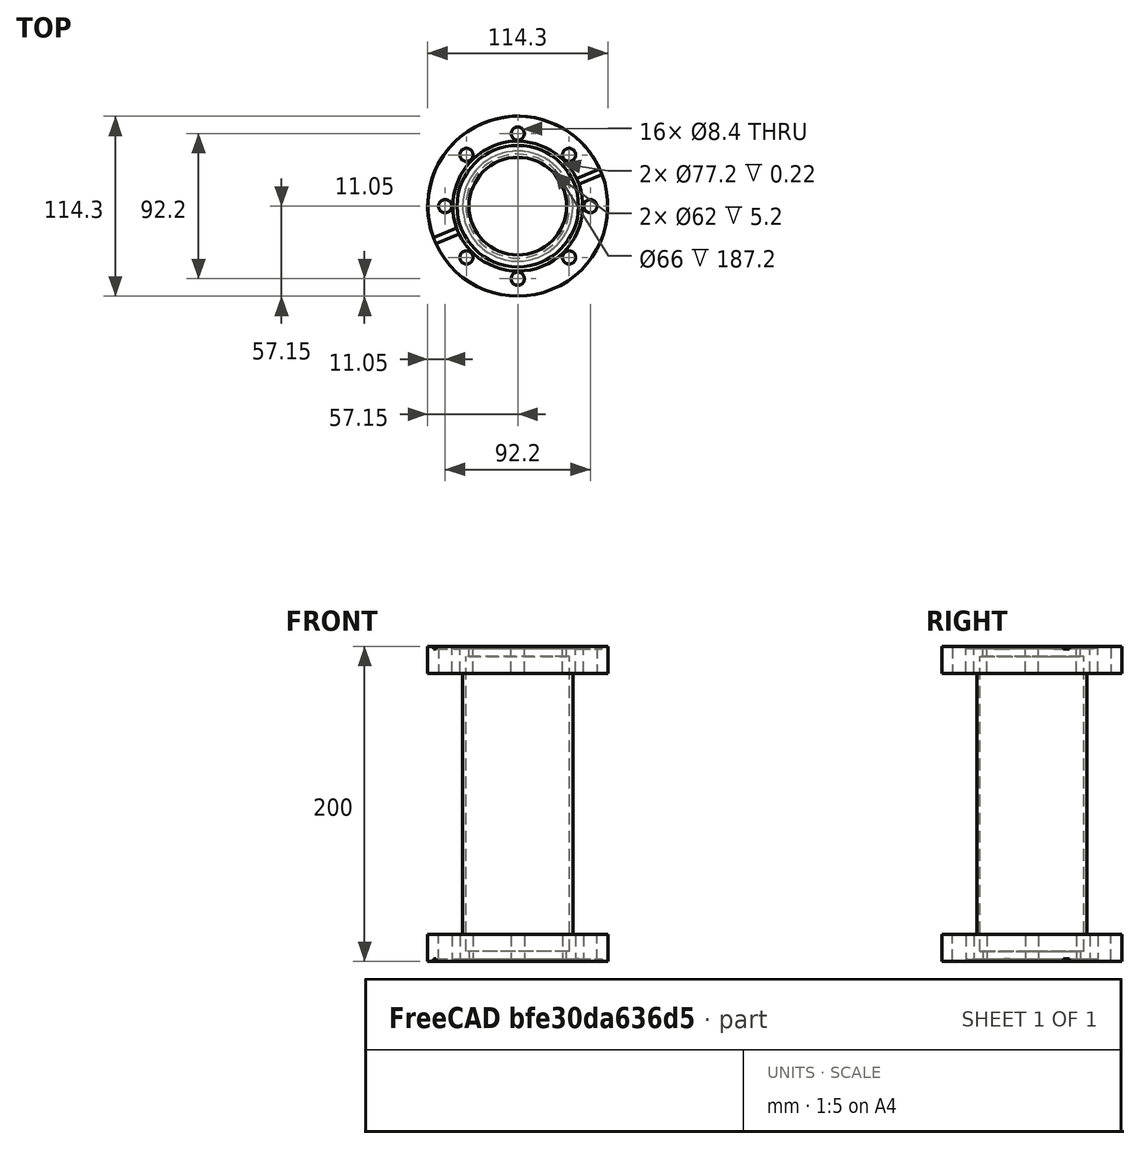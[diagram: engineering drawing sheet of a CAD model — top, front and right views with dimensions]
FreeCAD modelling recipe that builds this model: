
FCSTD DOCUMENT  (FreeCAD 0.21R0.21.2)
Label: CFPipeStraight_NonRotatable
License: All rights reserved
LicenseURL: http://en.wikipedia.org/wiki/All_rights_reserved
objects: Part::Cylinder×14, Part::Cut×12, Part::MultiFuse×7, Part::Box×4, Part::FeaturePython×3, Part::Cone×2, Spreadsheet::Sheet×1, Part::Compound×1
note: 41 computed .brp shape members not serialized (recipe doc carries the construction recipe); baked Part::Feature solids carry a one-line shape summary decoded from their .brp

FEATURE [Part::Box] Box002  label="Cube002"
  AttacherType = Attacher::AttachEngine3D
  Height = 1.5
  Length = 16.9
  Placement = pos=(40.75,-2,0) rot=(0,0,1;0rad)
  Width = 4
  expr: .Placement.Base.x = <<ConflatFlange>>.cf_sealrecess / 2 - 0.5
  expr: .Placement.Base.y = -2
  expr: Length = (<<ConflatFlange>>.cf_od - <<ConflatFlange>>.cf_sealrecess) / 2 + 1
FEATURE [Part::Box] Box003  label="Cube003"
  AttacherType = Attacher::AttachEngine3D
  Height = 1.5
  Length = 16.9
  Placement = pos=(-57.65,-2,0) rot=(0,0,1;0rad)
  Width = 4
  expr: .Placement.Base.x = -<<ConflatFlange>>.cf_sealrecess / 2 + 0.5 - ((<<ConflatFlange>>.cf_od - <<ConflatFlange>>.cf_sealrecess) / 2 + 1)
  expr: .Placement.Base.y = -2
  expr: Length = (<<ConflatFlange>>.cf_od - <<ConflatFlange>>.cf_sealrecess) / 2 + 1
FEATURE [Part::Cone] Cone004
  Angle = 360
  AttacherType = Attacher::AttachEngine3D
  Height = 0.22
  Radius1 = 38.6
  Radius2 = 41.25
  expr: Height = 1.2 - 0.98
  expr: Radius1 = <<ConflatFlange>>.cf_knife / 2
  expr: Radius2 = <<ConflatFlange>>.cf_sealrecess / 2
FEATURE [Part::Cylinder] Cylinder018
  Angle = 360
  AttacherType = Attacher::AttachEngine3D
  FirstAngle = 0
  Height = 10.6
  Placement = pos=(0,0,6.4) rot=(0,0,1;0rad)
  Radius = 35
  SecondAngle = 0
  expr: .Placement.Base.z = <<ConflatFlange>>.cf_pipedepth
  expr: Height = <<ConflatFlange>>.cf_thickness - <<ConflatFlange>>.cf_pipedepth
  expr: Radius = <<ConflatFlange>>.cf_maxtubedia / 2
FEATURE [Part::Cylinder] Cylinder019
  Angle = 360
  AttacherType = Attacher::AttachEngine3D
  FirstAngle = 0
  Height = 17
  Radius = 31
  SecondAngle = 0
  expr: Height = <<ConflatFlange>>.cf_thickness
  expr: Radius = <<ConflatFlange>>.cf_maxtubedia / 2 - 2 * <<ConflatFlange>>.cf_pipe_wallwidth
FEATURE [Part::Cylinder] Cylinder020  label="Blank004"
  Angle = 360
  AttacherType = Attacher::AttachEngine3D
  FirstAngle = 0
  Height = 17
  Radius = 57.15
  SecondAngle = 0
  expr: Height = <<ConflatFlange>>.cf_thickness
  expr: Radius = <<ConflatFlange>>.cf_od / 2
FEATURE [Part::Cylinder] Cylinder021  label="SealRecess004"
  Angle = 360
  AttacherType = Attacher::AttachEngine3D
  FirstAngle = 0
  Height = 1.2
  Radius = 41.25
  SecondAngle = 0
  expr: Radius = <<ConflatFlange>>.cf_sealrecess / 2
FEATURE [Part::Cut] Cut015
  Base = -> Cylinder020
  Tool = -> Cylinder021
FEATURE [Part::Cylinder] Cylinder022
  Angle = 360
  AttacherType = Attacher::AttachEngine3D
  FirstAngle = 0
  Height = 0.22
  Radius = 38.6
  SecondAngle = 0
  expr: Height = 1.2 - 0.98
  expr: Radius = <<ConflatFlange>>.cf_knife / 2
FEATURE [Part::Cut] Cut016  label="KnifeEdge004"
  Base = -> Cone004
  Placement = pos=(0,0,0.98) rot=(0,0,1;0rad)
  Tool = -> Cylinder022
FEATURE [Part::Cylinder] Cylinder023
  Angle = 360
  AttacherType = Attacher::AttachEngine3D
  FirstAngle = 0
  Height = 17
  Placement = pos=(46.1,0,0) rot=(0,0,1;0rad)
  Radius = 4.2
  SecondAngle = 0
  expr: .Placement.Base.x = <<ConflatFlange>>.cf_boltcircle / 2
  expr: Height = <<ConflatFlange>>.cf_thickness
  expr: Radius = <<ConflatFlange>>.cf_boltdia / 2
FEATURE [Part::FeaturePython] Array004  label="BoltHoleArray004"  # Draft array (typed FeaturePython)
  AlwaysSyncPlacement = false
  Angle = 360
  ArrayType = 1
  Axis = (0,0,1)
  Base = -> Cylinder023
  Center = (0,0,0)
  Count = 8
  ExpandArray = false
  Fuse = false
  IntervalAxis = (0,0,0)
  IntervalX = (50,0,0)
  IntervalY = (0,50,0)
  IntervalZ = (0,0,50)
  NumberCircles = 3
  NumberPolar = 8
  NumberX = 2
  NumberY = 2
  NumberZ = 1
  PlacementList = 8 placements: [(46.1,0,0),(32.5976,32.5976,0),(1.02363e-14,46.1,0),(-32.5976,32.5976,0),(-46.1,5.64562e-15,0),(-32.5976,-32.5976,0),(-1.02363e-14,-46.1,0),(32.5976,-32.5976,0)]
  RadialDistance = 50
  ScaleList = (8) [(1,1,1),(1,1,1),(1,1,1),(1,1,1),(1,1,1),(1,1,1),(1,1,1),(1,1,1)]
  Symmetry = 1
  TangentialDistance = 25
  expr: NumberPolar = <<ConflatFlange>>.cf_nbolts
FEATURE [Part::Cylinder] Cylinder025
  Angle = 360
  AttacherType = Attacher::AttachEngine3D
  FirstAngle = 0
  Height = 1.5
  Radius = 41.25
  SecondAngle = 0
  expr: Radius = <<ConflatFlange>>.cf_sealrecess / 2
FEATURE [Part::MultiFuse] Fusion005  label="UndrilledBlank004"
  Shapes = -> [Cut015,Cut016]
FEATURE [Part::Cut] Cut017  label="BlankFlange_NonRotatable002"
  Base = -> Fusion005
  Tool = -> Array004
FEATURE [Part::MultiFuse] Fusion006
  Shapes = -> [Cylinder019,Cylinder018]
FEATURE [Part::Cut] Cut018  label="WeldFlange_NonRotatable_NoGrooves"
  Base = -> Cut017
  Tool = -> Fusion006
FEATURE [Part::MultiFuse] Fusion008
  Placement = pos=(0,0,0) rot=(0,0,1;0.392699rad)
  Shapes = -> [Box003,Box002]
  expr: .Placement.Rotation.Angle = 360 / (<<ConflatFlange>>.cf_nbolts * 2)
FEATURE [Part::Cut] Cut021  label="LeakTestGrooves02"
  Base = -> Fusion008
  Tool = -> Cylinder025
FEATURE [Part::Cut] Cut024  label="WeldFlange_NonRotatable"
  Base = -> Cut018
  Tool = -> Cut021
FEATURE [Spreadsheet::Sheet] Spreadsheet  label="ConflatFlange"
  CF = 5
  cells = A1='CF; B1='Outside Diameter; C1='Maximum tube diameter; D1='Number of bolts; E1='Bolt hole diameter; F1='Tap hole diameter; G1='Bolt Thread (metric); H1='Bot inclination; I1='Bolt Circle; J1='Bolt position tolerance; K1='Seal recess; L1='Knife edge; M1='Pipe attachment depth; N1='Setback (inner rotatable); O1='Thickness; Q1='Calculated Quantities; A2==hiddenref(.CF.String); B2(cf_od)==.B8; C2(cf_maxtubedia)==.C8; D2(cf_nbolts)==.D8; E2(cf_boltdia)==.E8; F2(cf_tapdia)==.F8; G2(cf_boltm)==.G8; H2(cf_boltinclination)==.H8; I2(cf_boltcircle)==.I8; J2(cf_bolttolerance)==.J8; K2(cf_sealrecess)==.K8; L2(cf_knife)==.L8; M2(cf_pipedepth)==.M8; N2(cf_setbackrot)==.N8; O2(cf_thickness)==.O8; Q2='Knife edge width; R2(cf__kfwidth)==(cf_sealrecess - cf_knife) / 2; A3='10; B3=25; C3=12; D3=6; E3=3.3; F3=2.39; G3=3; H3=0.5; I3=17.6; J3=0.1; K3=13.5; L3=10.5; M3=3; N3=0; O3=6; Q3='Knife height; R3(cf__kfheight)==tan(20 * 3.14 / 180) * cf__kfwidth; A4='16; B4=33.8; C4=19.4; D4=6; E4=4.4; F4=3.14; G4=4; H4=0.7; I4=27; J4=0.1; K4=21.4; L4=18.3; M4=3.3; N4=5.9; O4=7; A5='25; B5=54; C5=25.8; D5=4; E5=6.8; F5=4.77; G5=6; H5=1; I5=41.3; J5=0.2; K5=33; L5=27.7; M5=4.3; N5=6; O5=11.5; A6='40; B6=69.9; C6=44.5; D6=6; E6=6.8; F6=4.77; G6=6; H6=1; I6=58.7; J6=0.2; K6=48.3; L6=41.9; M6=4.3; N6=7.7; O6=12.5; A7='50; B7=85.7; C7=51; D7=8; E7=8.4; F7=6.47; G7=8; H7=1.25; I7=72.4; J7=0.2; K7=61.8; L7=55.9; M7=4.9; N7=9.7; O7=16; A8='63; B8=114.3; C8=70; D8=8; E8=8.4; F8=6.47; G8=8; H8=1.25; I8=92.2; J8=0.2; K8=82.5; L8=77.2; M8=6.4; N8=12.7; O8=17; A9='75; B9=117.4; C9=76.2; D9=10; E9=8.4; F9=6.47; G9=8; H9=1.25; I9=102.3; J9=0.2; K9=91.6; L9=85.2; M9=6.5; N9=13; O9=17.5; A10='100; B10=152.4; C10=108; D10=16; E10=8.4; F10=6.47; G10=8; H10=1.25; I10=130.3; J10=0.2; K10=120.6; L10=115.3; M10=7.2; N10=14.3; O10=19.5; A11='125; B11=171.5; C11=127; D11=18; E11=8.4; F11=6.47; G11=8; H11=1.25; I11=151.6; J11=0.2; K11=141.8; L11=136.3; M11=7.2; N11=14.3; O11=21; A12='160; B12=203.2; C12=159; D12=20; E12=8.4; F12=6.47; G12=8; H12=1.25; I12=181; J12=0.2; K12=171.4; L12=166.1; M12=8; N12=15.9; O12=21; A13='200; B13=254; C13=206; D13=24; E13=8.4; F13=6.47; G13=8; H13=1.25; I13=231.8; J13=0.2; K13=222.2; L13=216.9; M13=8.6; N13=17.2; O13=24; +88 more cells
  expr: .CF.Enum = cells[<<A3:|>>]
  expr: .cells.Bind.B2.O2 = tuple(.cells; <<B>> + str(hiddenref(CF) + 3); <<O>> + str(hiddenref(CF) + 3))
FEATURE [Part::Box] Box004  label="Cube004"
  AttacherType = Attacher::AttachEngine3D
  Height = 1.5
  Length = 16.9
  Placement = pos=(40.75,-2,0) rot=(0,0,1;0rad)
  Width = 4
  expr: .Placement.Base.x = <<ConflatFlange>>.cf_sealrecess / 2 - 0.5
  expr: .Placement.Base.y = -2
  expr: Length = (<<ConflatFlange>>.cf_od - <<ConflatFlange>>.cf_sealrecess) / 2 + 1
FEATURE [Part::Box] Box005  label="Cube005"
  AttacherType = Attacher::AttachEngine3D
  Height = 1.5
  Length = 16.9
  Placement = pos=(-57.65,-2,0) rot=(0,0,1;0rad)
  Width = 4
  expr: .Placement.Base.x = -<<ConflatFlange>>.cf_sealrecess / 2 + 0.5 - ((<<ConflatFlange>>.cf_od - <<ConflatFlange>>.cf_sealrecess) / 2 + 1)
  expr: .Placement.Base.y = -2
  expr: Length = (<<ConflatFlange>>.cf_od - <<ConflatFlange>>.cf_sealrecess) / 2 + 1
FEATURE [Part::Cone] Cone005
  Angle = 360
  AttacherType = Attacher::AttachEngine3D
  Height = 0.22
  Radius1 = 38.6
  Radius2 = 41.25
  expr: Height = 1.2 - 0.98
  expr: Radius1 = <<ConflatFlange>>.cf_knife / 2
  expr: Radius2 = <<ConflatFlange>>.cf_sealrecess / 2
FEATURE [Part::Cylinder] Cylinder026
  Angle = 360
  AttacherType = Attacher::AttachEngine3D
  FirstAngle = 0
  Height = 10.6
  Placement = pos=(0,0,6.4) rot=(0,0,1;0rad)
  Radius = 35
  SecondAngle = 0
  expr: .Placement.Base.z = <<ConflatFlange>>.cf_pipedepth
  expr: Height = <<ConflatFlange>>.cf_thickness - <<ConflatFlange>>.cf_pipedepth
  expr: Radius = <<ConflatFlange>>.cf_maxtubedia / 2
FEATURE [Part::Cylinder] Cylinder027
  Angle = 360
  AttacherType = Attacher::AttachEngine3D
  FirstAngle = 0
  Height = 17
  Radius = 31
  SecondAngle = 0
  expr: Height = <<ConflatFlange>>.cf_thickness
  expr: Radius = <<ConflatFlange>>.cf_maxtubedia / 2 - 2 * <<ConflatFlange>>.cf_pipe_wallwidth
FEATURE [Part::Cylinder] Cylinder028  label="Blank005"
  Angle = 360
  AttacherType = Attacher::AttachEngine3D
  FirstAngle = 0
  Height = 17
  Radius = 57.15
  SecondAngle = 0
  expr: Height = <<ConflatFlange>>.cf_thickness
  expr: Radius = <<ConflatFlange>>.cf_od / 2
FEATURE [Part::Cylinder] Cylinder029  label="SealRecess005"
  Angle = 360
  AttacherType = Attacher::AttachEngine3D
  FirstAngle = 0
  Height = 1.2
  Radius = 41.25
  SecondAngle = 0
  expr: Radius = <<ConflatFlange>>.cf_sealrecess / 2
FEATURE [Part::Cut] Cut025
  Base = -> Cylinder028
  Tool = -> Cylinder029
FEATURE [Part::Cylinder] Cylinder030
  Angle = 360
  AttacherType = Attacher::AttachEngine3D
  FirstAngle = 0
  Height = 0.22
  Radius = 38.6
  SecondAngle = 0
  expr: Height = 1.2 - 0.98
  expr: Radius = <<ConflatFlange>>.cf_knife / 2
FEATURE [Part::Cut] Cut026  label="KnifeEdge005"
  Base = -> Cone005
  Placement = pos=(0,0,0.98) rot=(0,0,1;0rad)
  Tool = -> Cylinder030
FEATURE [Part::Cylinder] Cylinder031
  Angle = 360
  AttacherType = Attacher::AttachEngine3D
  FirstAngle = 0
  Height = 17
  Placement = pos=(46.1,0,0) rot=(0,0,1;0rad)
  Radius = 4.2
  SecondAngle = 0
  expr: .Placement.Base.x = <<ConflatFlange>>.cf_boltcircle / 2
  expr: Height = <<ConflatFlange>>.cf_thickness
  expr: Radius = <<ConflatFlange>>.cf_boltdia / 2
FEATURE [Part::FeaturePython] Array005  label="BoltHoleArray005"  # Draft array (typed FeaturePython)
  AlwaysSyncPlacement = false
  Angle = 360
  ArrayType = 1
  Axis = (0,0,1)
  Base = -> Cylinder031
  Center = (0,0,0)
  Count = 8
  ExpandArray = false
  Fuse = false
  IntervalAxis = (0,0,0)
  IntervalX = (50,0,0)
  IntervalY = (0,50,0)
  IntervalZ = (0,0,50)
  NumberCircles = 3
  NumberPolar = 8
  NumberX = 2
  NumberY = 2
  NumberZ = 1
  PlacementList = 8 placements: [(46.1,0,0),(32.5976,32.5976,0),(1.02363e-14,46.1,0),(-32.5976,32.5976,0),(-46.1,5.64562e-15,0),(-32.5976,-32.5976,0),(-1.02363e-14,-46.1,0),(32.5976,-32.5976,0)]
  RadialDistance = 50
  ScaleList = (8) [(1,1,1),(1,1,1),(1,1,1),(1,1,1),(1,1,1),(1,1,1),(1,1,1),(1,1,1)]
  Symmetry = 1
  TangentialDistance = 25
  expr: NumberPolar = <<ConflatFlange>>.cf_nbolts
FEATURE [Part::Cylinder] Cylinder032
  Angle = 360
  AttacherType = Attacher::AttachEngine3D
  FirstAngle = 0
  Height = 1.5
  Radius = 41.25
  SecondAngle = 0
  expr: Radius = <<ConflatFlange>>.cf_sealrecess / 2
FEATURE [Part::MultiFuse] Fusion009  label="UndrilledBlank005"
  Shapes = -> [Cut025,Cut026]
FEATURE [Part::Cut] Cut027  label="BlankFlange_NonRotatable003"
  Base = -> Fusion009
  Tool = -> Array005
FEATURE [Part::MultiFuse] Fusion010
  Shapes = -> [Cylinder027,Cylinder026]
FEATURE [Part::Cut] Cut028  label="WeldFlange_NonRotatable_NoGrooves001"
  Base = -> Cut027
  Tool = -> Fusion010
FEATURE [Part::MultiFuse] Fusion011
  Placement = pos=(0,0,0) rot=(0,0,1;0.392699rad)
  Shapes = -> [Box005,Box004]
  expr: .Placement.Rotation.Angle = 360 / (<<ConflatFlange>>.cf_nbolts * 2)
FEATURE [Part::Cut] Cut029  label="LeakTestGrooves003"
  Base = -> Fusion011
  Tool = -> Cylinder032
FEATURE [Part::Cut] Cut030  label="WeldFlange_NonRotatable001"
  Base = -> Cut028
  Placement = pos=(0,0,200) rot=(1,0,0;3.14159rad)
  Tool = -> Cut029
  expr: .Placement.Base.z = <<ConflatFlange>>.pipe_flange_to_flange
FEATURE [Part::FeaturePython] Tube  # WARN: FeaturePython — macro-defined, semantics opaque (R4)
  AttacherType = Attacher::AttachEngine3D
  Height = 187.2
  InnerRadius = 33
  OuterRadius = 35
  Placement = pos=(0,0,6.4) rot=(1,0,0;0rad)
  expr: .Placement.Base.z = <<ConflatFlange>>.cf_pipedepth
  expr: Height = <<ConflatFlange>>.pipe_flange_to_flange - 2 * <<ConflatFlange>>.cf_pipedepth
  expr: InnerRadius = <<ConflatFlange>>.cf_pipe_dia / 2 - <<ConflatFlange>>.cf_pipe_wallwidth
  expr: OuterRadius = <<ConflatFlange>>.cf_pipe_dia / 2
FEATURE [Part::Compound] Compound  label="LeakTestGrooveAlignmentRotation"
  Links = -> [Cut030]
  Placement = pos=(0,0,0) rot=(0,0,1;0.785398rad)
  expr: .Placement.Rotation.Angle = 360 / <<ConflatFlange>>.cf_nbolts
FEATURE [Part::MultiFuse] Fusion  label="CFPipeStraigt_NR"
  Shapes = -> [Cut024,Compound,Tube]
